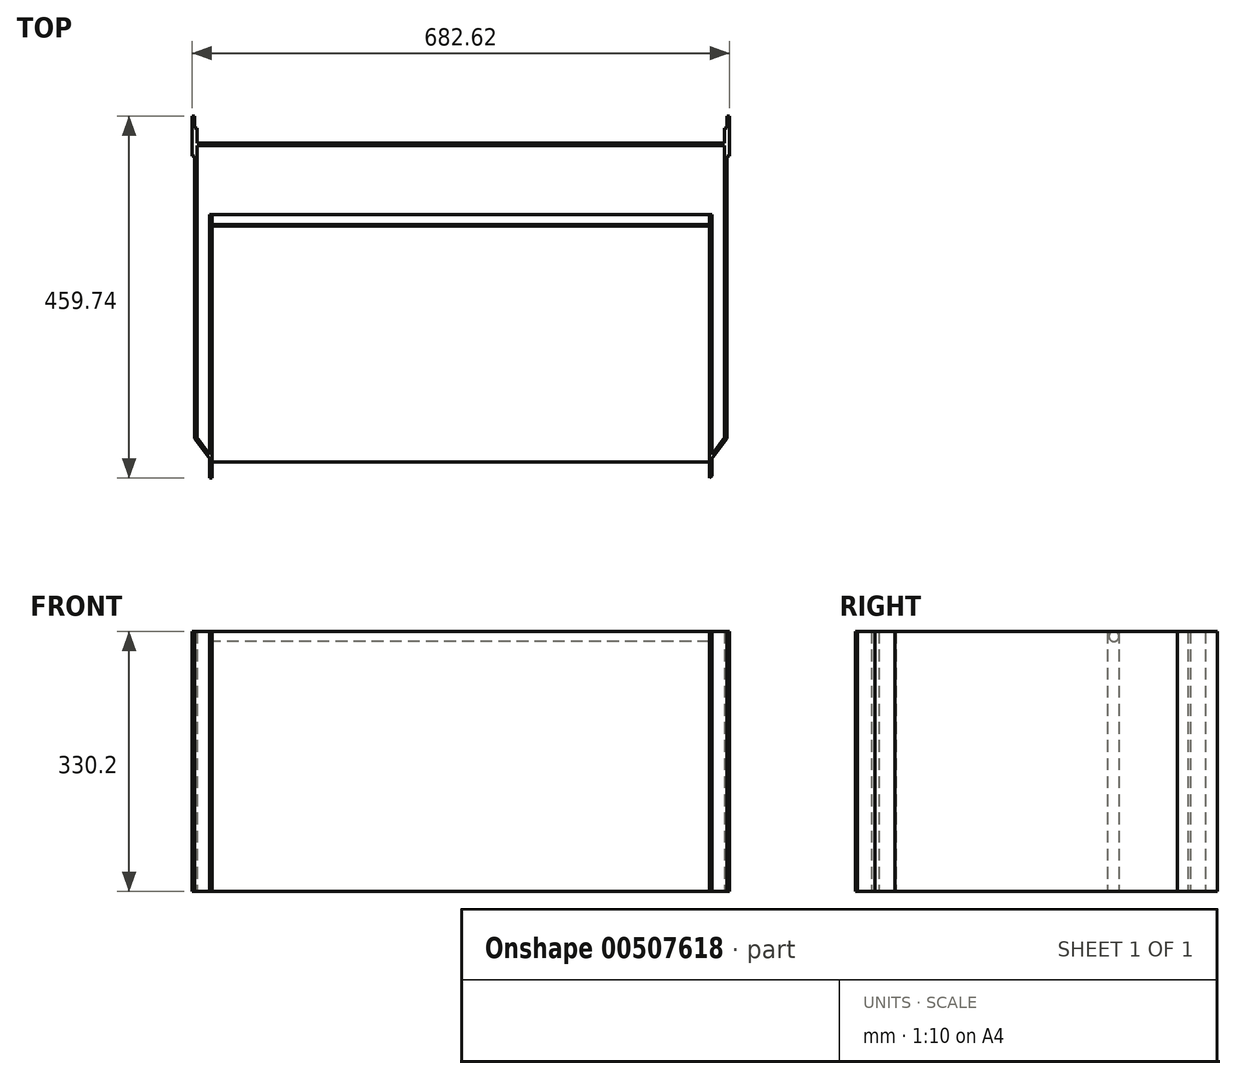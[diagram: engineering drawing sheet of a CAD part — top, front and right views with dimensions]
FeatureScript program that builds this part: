
annotation { "Feature Type Name" : "Feature", "Feature Type Description" : "" }
export const myFeature = defineFeature(function(context is Context, id is Id, definition is map)
    precondition{}
    {
        {
            var Q0;
            Q0=qCreatedBy(makeId("Top.planeOp"),FACE);
            var sketch = newSketch(context, id + "F0", { "sketchPlane" : qUnion([Q0])});
            skLineSegment(sketch, "E0.left", {"start": v(-338.14, 219.83) * mm, "end": v(-338.14, -174.3) * mm});
            skLineSegment(sketch, "E0.right", {"start": v(338.14, 219.83) * mm, "end": v(338.14, -174.3) * mm});
            skPoint(sketch, "E0.middle", {"position": v(0, 0) * mm});
            skLineSegment(sketch, "E1", {"start": v(-319.09, 110.1) * mm, "end": v(-319.09, -194.7) * mm, "construction": true});
            skLineSegment(sketch, "E2", {"start": v(-338.14, -200.03) * mm, "end": v(338.14, -200.02) * mm, "construction": true});
            skLineSegment(sketch, "E3", {"start": v(-319.09, -200.03) * mm, "end": v(-338.14, -174.3) * mm});
            skLineSegment(sketch, "E4", {"start": v(-319.09, -200.03) * mm, "end": v(-319.09, -222.25) * mm});
            skLineSegment(sketch, "E5.bottom", {"start": v(-319.09, 219.83) * mm, "end": v(-315.91, 219.83) * mm});
            skLineSegment(sketch, "E5.top", {"start": v(-319.09, -224.67) * mm, "end": v(-315.91, -224.67) * mm});
            skLineSegment(sketch, "E5.left", {"start": v(-319.09, 110.1) * mm, "end": v(-319.09, -194.7) * mm});
            skLineSegment(sketch, "E5.right", {"start": v(-315.91, 110.1) * mm, "end": v(-315.91, -224.67) * mm});
            skLineSegment(sketch, "E6.0", {"start": v(-319.09, -194.7) * mm, "end": v(-334.96, -173.25) * mm});
            skLineSegment(sketch, "E6.1", {"start": v(-334.96, 219.83) * mm, "end": v(-334.96, 200.78) * mm});
            skLineSegment(sketch, "E7", {"start": v(-319.09, 110.1) * mm, "end": v(-315.91, 110.1) * mm});
            skLineSegment(sketch, "E8.MirrorCS", {"start": v(315.91, 110.1) * mm, "end": v(315.91, -224.67) * mm});
            skLineSegment(sketch, "E9.MirrorCS", {"start": v(319.09, -200.03) * mm, "end": v(319.09, -222.25) * mm, "construction": true});
            skLineSegment(sketch, "E10.MirrorCS", {"start": v(334.96, 219.83) * mm, "end": v(334.96, 200.78) * mm});
            skLineSegment(sketch, "E11.MirrorCS", {"start": v(319.09, -194.7) * mm, "end": v(334.96, -173.25) * mm});
            skLineSegment(sketch, "E12.MirrorCS", {"start": v(319.09, -200.03) * mm, "end": v(338.14, -174.3) * mm});
            skLineSegment(sketch, "E13.MirrorCS", {"start": v(319.09, 110.1) * mm, "end": v(319.09, -222.25) * mm});
            skLineSegment(sketch, "E14.MirrorCS", {"start": v(319.09, 110.1) * mm, "end": v(315.91, 110.1) * mm});
            skLineSegment(sketch, "E15", {"start": v(-319.09, -222.25) * mm, "end": v(-315.91, -224.67) * mm});
            skPoint(sketch, "E16.orphan", {"position": v(-316.54, -198.14) * mm});
            skLineSegment(sketch, "E17.trimOffspring", {"start": v(-319.09, -200.03) * mm, "end": v(-319.09, -222.25) * mm, "construction": true});
            skLineSegment(sketch, "E18.trimOffspring", {"start": v(-319.09, -200.03) * mm, "end": v(-319.09, -224.67) * mm});
            skPoint(sketch, "E19.orphan", {"position": v(319.09, 110.1) * mm});
            skLineSegment(sketch, "E20.trimOffspring", {"start": v(319.09, -194.7) * mm, "end": v(319.09, -222.25) * mm, "construction": true});
            skLineSegment(sketch, "E21", {"start": v(315.91, -224.67) * mm, "end": v(319.09, -222.25) * mm});
            skPoint(sketch, "E22.orphan", {"position": v(338.14, -222.25) * mm});
            skPoint(sketch, "E23.orphan", {"position": v(316.54, -198.14) * mm});
            skLineSegment(sketch, "E24", {"start": v(338.14, 219.83) * mm, "end": v(334.96, 219.83) * mm});
            skLineSegment(sketch, "E25", {"start": v(-334.96, 219.83) * mm, "end": v(-315.91, 219.83) * mm, "construction": true});
            skLineSegment(sketch, "E26", {"start": v(334.96, 219.83) * mm, "end": v(-334.96, 219.83) * mm, "construction": true});
            skLineSegment(sketch, "E27", {"start": v(-315.91, -224.67) * mm, "end": v(315.91, -224.67) * mm, "construction": true});
            skLineSegment(sketch, "E28", {"start": v(-334.96, 200.78) * mm, "end": v(334.96, 200.78) * mm});
            skLineSegment(sketch, "E29", {"start": v(-334.96, 197.62) * mm, "end": v(334.96, 197.62) * mm});
            skLineSegment(sketch, "E30.trimOffspring", {"start": v(-334.96, 197.62) * mm, "end": v(-334.96, -173.25) * mm});
            skLineSegment(sketch, "E31.trimOffspring", {"start": v(334.96, 197.62) * mm, "end": v(334.96, -173.25) * mm});
            skLineSegment(sketch, "E32", {"start": v(-334.96, 219.83) * mm, "end": v(-338.14, 219.83) * mm});
            skPoint(sketch, "E33.orphan", {"position": v(-338.14, 222.25) * mm});
            skPoint(sketch, "E34.orphan", {"position": v(338.14, 222.25) * mm});
            skSolve(sketch);
        }
        {
            var Q0;
            Q0=makeQuery(id+"F0.imprint","IMPRINT",FACE,{"disambiguationData":[TD([[makeQuery(id+"F0.imprint","IMPRINT",EDGE,{"derivedFrom":sQuery(id+"F0.wireOp",EDGE,"E0.left")}),1.0]])]});
            var Q1;
            {var subQ2=sQuery(id+"F0.wireOp",EDGE,"E5.top");Q1=makeQuery(id+"F0.imprint","IMPRINT",FACE,{"disambiguationData":[TD([[makeQuery(id+"F0.imprint","IMPRINT",EDGE,{"derivedFrom":subQ2}),1.0]])]});}
            var Q2;
            Q2=makeQuery(id+"F0.imprint","IMPRINT",FACE,{"disambiguationData":[TD([[makeQuery(id+"F0.imprint","IMPRINT",EDGE,{"derivedFrom":sQuery(id+"F0.wireOp",EDGE,"E8.MirrorCS")}),1.0]])]});
            var Q3;
            Q3=makeQuery(id+"F0.imprint","IMPRINT",FACE,{"disambiguationData":[TD([[makeQuery(id+"F0.imprint","IMPRINT",EDGE,{"derivedFrom":sQuery(id+"F0.wireOp",EDGE,"E10.MirrorCS")}),1.0]])]});
            extrude(context, id + "F1", {"entities" : qUnion([Q0, Q1, Q2, Q3]), "depth" : 330.2 * mm, "offsetDistance" : 25.4 * mm});
        }
        {
            var Q0;
            Q0=makeQuery(id+"F1.opExtrude","SWEPT_FACE",FACE,{"disambiguationData":[OSD([sQuery(id+"F0.wireOp",EDGE,"E5.right")])]});
            var sketch = newSketch(context, id + "F2", { "sketchPlane" : qUnion([Q0])});
            skPoint(sketch, "E35", {"position": v(103.76, 323.85) * mm});
            skCircle(sketch, "E36", {"center": v(103.76, 323.85) * mm, "radius": 6.35 * mm});
            skSolve(sketch);
        }
        {
            var Q0;
            {var subQ0=sQuery(id+"F2.wireOp",EDGE,"E36");var subQ1=sQuery(id+"F0.wireOp",EDGE,"E5.right");var subQ3=makeQuery(id+"F2.imprint","INTERSECT",VERTEX,{"derivedFrom":[makeQuery(id+"F1.opExtrude","CAP_EDGE",EDGE,{"disambiguationData":[OSD([subQ1])],"isStart":false}),subQ0]});Q0=makeQuery(id+"F2.imprint","IMPRINT",FACE,{"disambiguationData":[TD([[makeQuery(id+"F2.imprint","IMPRINT",EDGE,{"disambiguationData":[TD([[subQ3,1.0]])],"derivedFrom":subQ0}),1.0]])]});}
            var Q1;
            Q1=makeQuery(id+"F1.opExtrude","SWEPT_FACE",FACE,{"disambiguationData":[OSD([sQuery(id+"F0.wireOp",EDGE,"E8.MirrorCS")])]});
            extrude(context, id + "F3", {"entities" : qUnion([Q0]), "endBound" : BoundingType.UP_TO_SURFACE, "depth" : 25.4 * mm, "endBoundEntityFace" : qUnion([Q1]), "offsetDistance" : 25.4 * mm, "offsetOppositeDirection" : true});
        }
        {
            var Q0;
            Q0=makeQuery(id+"F1.opExtrude","SWEPT_FACE",FACE,{"disambiguationData":[OSD([sQuery(id+"F0.wireOp",EDGE,"E5.right")])]});
            var sketch = newSketch(context, id + "F4", { "sketchPlane" : qUnion([Q0])});
            skLineSegment(sketch, "E37.bottom", {"start": v(110.1, 330.2) * mm, "end": v(103.76, 330.2) * mm});
            skLineSegment(sketch, "E37.top", {"start": v(95.53, 0) * mm, "end": v(-204.13, 0) * mm});
            skLineSegment(sketch, "E37.right", {"start": v(-204.13, 330.2) * mm, "end": v(-204.13, 0) * mm});
            skLineSegment(sketch, "E38.0", {"start": v(-194.7, 330.2) * mm, "end": v(-194.7, 330.2) * mm});
            skLineSegment(sketch, "E39.0", {"start": v(110.1, 330.2) * mm, "end": v(110.1, 323.85) * mm});
            skLineSegment(sketch, "E40", {"start": v(110.1, 330.2) * mm, "end": v(110.1, 0) * mm});
            skCircle(sketch, "E41.0", {"center": v(103.76, 323.85) * mm, "radius": 6.35 * mm});
            skLineSegment(sketch, "E42", {"start": v(95.53, 330.2) * mm, "end": v(95.53, 0) * mm});
            skLineSegment(sketch, "E43.trimOffspring", {"start": v(95.53, 330.2) * mm, "end": v(-204.13, 330.2) * mm});
            skSolve(sketch);
        }
        {
            var Q0;
            Q0 = qSketchRegion(id + "F4", true);
            extrude(context, id + "F5", {"entities" : qUnion([Q0]), "endBound" : BoundingType.UP_TO_NEXT, "depth" : 25.4 * mm, "offsetDistance" : 25.4 * mm});
        }
        {
            var Q0;
            Q0=makeQuery(id+"F1.opExtrude","SWEPT_FACE",FACE,{"disambiguationData":[OSD([sQuery(id+"F0.wireOp",EDGE,"E0.left")])]});
            var sketch = newSketch(context, id + "F6", { "sketchPlane" : qUnion([Q0])});
            skLineSegment(sketch, "E44.bottom", {"start": v(-184.27, 0) * mm, "end": v(-235.07, 0) * mm});
            skLineSegment(sketch, "E44.top", {"start": v(-184.27, 330.2) * mm, "end": v(-235.07, 330.2) * mm});
            skLineSegment(sketch, "E44.left", {"start": v(-184.27, 0) * mm, "end": v(-184.27, 330.2) * mm});
            skLineSegment(sketch, "E44.right", {"start": v(-235.07, 0) * mm, "end": v(-235.07, 330.2) * mm});
            skSolve(sketch);
        }
        {
            var Q0;
            {var subQ3=sQuery(id+"F6.wireOp",EDGE,"E44.left");Q0=makeQuery(id+"F6.imprint","IMPRINT",FACE,{"disambiguationData":[TD([[makeQuery(id+"F6.imprint","IMPRINT",EDGE,{"derivedFrom":subQ3}),1.0]])]});}
            var Q1;
            {var subQ2=sQuery(id+"F6.wireOp",EDGE,"E44.right");Q1=makeQuery(id+"F6.imprint","IMPRINT",FACE,{"disambiguationData":[TD([[makeQuery(id+"F6.imprint","IMPRINT",EDGE,{"derivedFrom":subQ2}),-1.0]])]});}
            extrude(context, id + "F7", {"entities" : qUnion([Q0, Q1]), "depth" : 3.17 * mm, "offsetDistance" : 25.4 * mm});
        }
        {
            var Q0;
            Q0=makeQuery(id+"F7.opExtrude","SWEPT_BODY",BODY,{"disambiguationData":[OSD([sQuery(id+"F6.wireOp",EDGE,"E44.bottom"),sQuery(id+"F6.wireOp",EDGE,"E44.top"),sQuery(id+"F6.wireOp",EDGE,"E44.left"),sQuery(id+"F6.wireOp",EDGE,"E44.right")])]});
            var Q1;
            Q1=qCreatedBy(makeId("Right.planeOp"),FACE);
            mirror(context, id + "F8", {"operationType" : NewBodyOperationType.ADD, "entities" : qUnion([Q0]), "mirrorPlane" : qUnion([Q1])});
        }
    });
